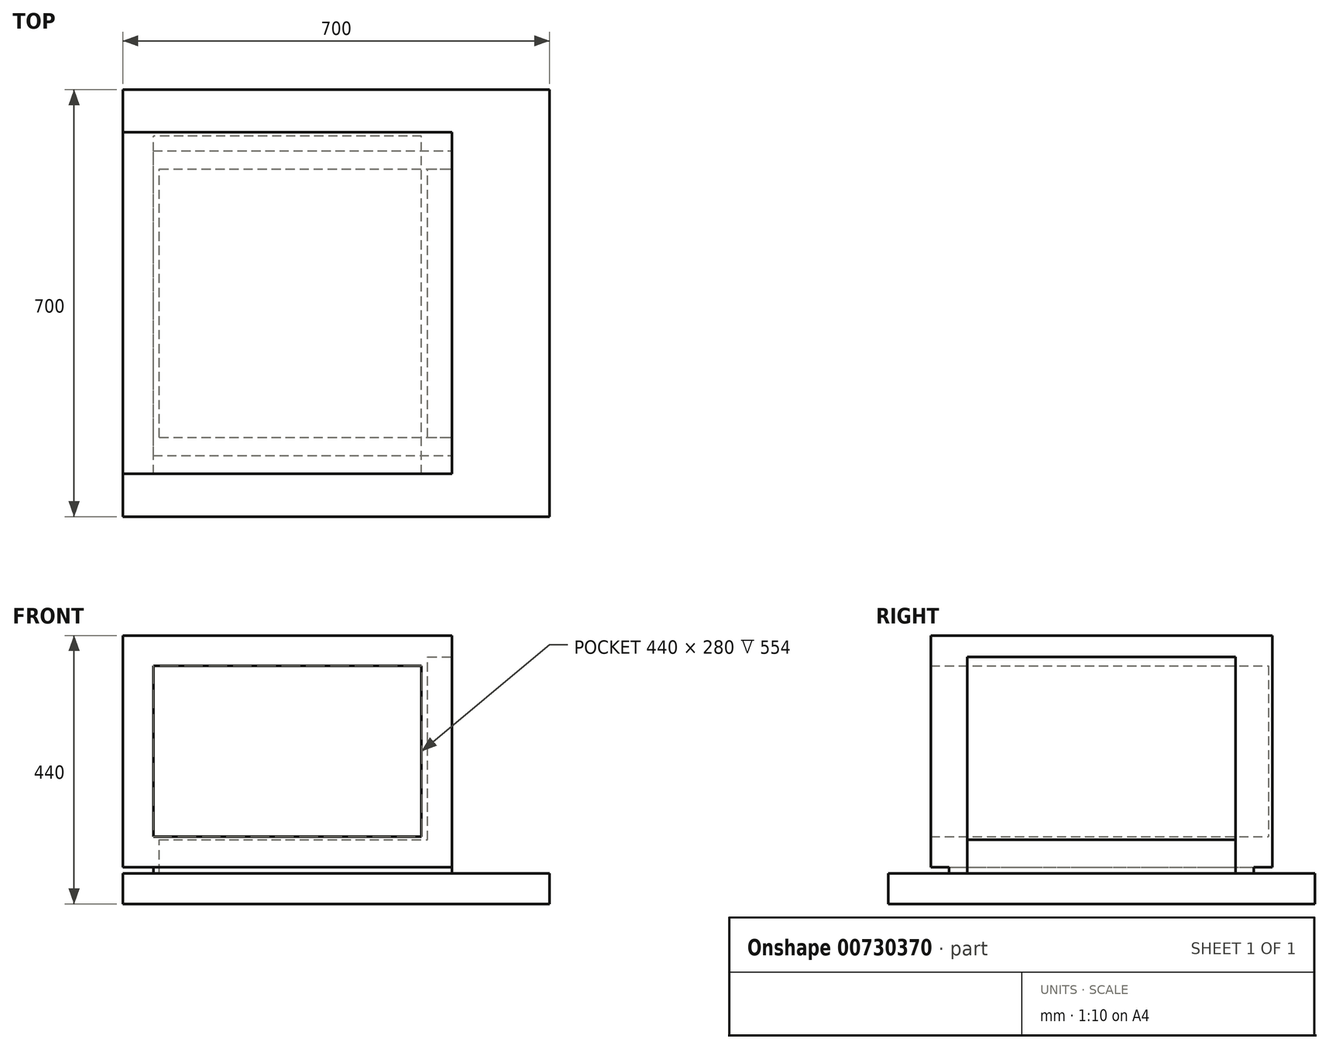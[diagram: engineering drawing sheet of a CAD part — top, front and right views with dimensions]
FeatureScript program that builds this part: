
annotation { "Feature Type Name" : "Feature", "Feature Type Description" : "" }
export const myFeature = defineFeature(function(context is Context, id is Id, definition is map)
    precondition{}
    {
        {
            var Q0;
            Q0=qCreatedBy(makeId("Front.planeOp"),FACE);
            var sketch = newSketch(context, id + "F0", { "sketchPlane" : qUnion([Q0])});
            skLineSegment(sketch, "E0.bottom", {"start": v(-270, 190) * mm, "end": v(270, 190) * mm});
            skLineSegment(sketch, "E0.top", {"start": v(-270, -190) * mm, "end": v(270, -190) * mm});
            skLineSegment(sketch, "E0.left", {"start": v(-270, 190) * mm, "end": v(-270, -190) * mm});
            skLineSegment(sketch, "E0.right", {"start": v(270, 190) * mm, "end": v(270, -190) * mm});
            skPoint(sketch, "E0.middle", {"position": v(0, 0) * mm});
            skLineSegment(sketch, "E1.bottom", {"start": v(220, 140) * mm, "end": v(-220, 140) * mm});
            skLineSegment(sketch, "E1.top", {"start": v(220, -140) * mm, "end": v(-220, -140) * mm});
            skLineSegment(sketch, "E1.left", {"start": v(220, 140) * mm, "end": v(220, -140) * mm});
            skLineSegment(sketch, "E1.right", {"start": v(-220, 140) * mm, "end": v(-220, -140) * mm});
            skSolve(sketch);
        }
        {
            var Q0;
            Q0 = qSketchRegion(id + "F0", true);
            extrude(context, id + "F1", {"entities" : qUnion([Q0]), "depth" : 560 * mm, "offsetDistance" : 25 * mm});
        }
        {
            var Q0;
            Q0=makeQuery(id+"F1.opExtrude","SWEPT_FACE",FACE,{"disambiguationData":[OSD([sQuery(id+"F0.wireOp",EDGE,"E0.top")])]});
            var sketch = newSketch(context, id + "F2", { "sketchPlane" : qUnion([Q0])});
            skLineSegment(sketch, "E2.bottom", {"start": v(-220, 530) * mm, "end": v(270, 530) * mm});
            skLineSegment(sketch, "E2.top", {"start": v(-220, 30) * mm, "end": v(270, 30) * mm});
            skLineSegment(sketch, "E2.left", {"start": v(-220, 530) * mm, "end": v(-220, 30) * mm});
            skLineSegment(sketch, "E2.right", {"start": v(270, 530) * mm, "end": v(270, 30) * mm});
            skSolve(sketch);
        }
        {
            var Q0;
            Q0 = qSketchRegion(id + "F2", true);
            extrude(context, id + "F3", {"entities" : qUnion([Q0]), "operationType" : NewBodyOperationType.ADD, "depth" : 10 * mm, "offsetDistance" : 25 * mm});
        }
        {
            var Q0;
            Q0=makeQuery(id+"F3.opExtrude","CAP_FACE",FACE,{"disambiguationData":[OSD([sQuery(id+"F2.wireOp",EDGE,"E2.bottom"),sQuery(id+"F2.wireOp",EDGE,"E2.top"),sQuery(id+"F2.wireOp",EDGE,"E2.left"),sQuery(id+"F2.wireOp",EDGE,"E2.right")])],"isStart":false});
            var sketch = newSketch(context, id + "F4", { "sketchPlane" : qUnion([Q0])});
            skLineSegment(sketch, "E3.bottom", {"start": v(-270, 630) * mm, "end": v(430, 630) * mm});
            skLineSegment(sketch, "E3.top", {"start": v(-270, -70) * mm, "end": v(430, -70) * mm});
            skLineSegment(sketch, "E3.left", {"start": v(-270, 630) * mm, "end": v(-270, -70) * mm});
            skLineSegment(sketch, "E3.right", {"start": v(430, 630) * mm, "end": v(430, -70) * mm});
            skLineSegment(sketch, "E4", {"start": v(270, 630) * mm, "end": v(270, 530) * mm, "construction": true});
            skLineSegment(sketch, "E5", {"start": v(270, 30) * mm, "end": v(270, -70) * mm, "construction": true});
            skSolve(sketch);
        }
        {
            var Q0;
            Q0 = qSketchRegion(id + "F4", true);
            extrude(context, id + "F5", {"entities" : qUnion([Q0]), "operationType" : NewBodyOperationType.ADD, "depth" : 50 * mm, "offsetDistance" : 25 * mm});
        }
        {
            var Q0;
            Q0=makeQuery(id+"F1.opExtrude","CAP_FACE",FACE,{"disambiguationData":[OSD([sQuery(id+"F0.wireOp",EDGE,"E0.bottom"),sQuery(id+"F0.wireOp",EDGE,"E0.top"),sQuery(id+"F0.wireOp",EDGE,"E0.left"),sQuery(id+"F0.wireOp",EDGE,"E0.right"),sQuery(id+"F0.wireOp",EDGE,"E1.bottom"),sQuery(id+"F0.wireOp",EDGE,"E1.top"),sQuery(id+"F0.wireOp",EDGE,"E1.left"),sQuery(id+"F0.wireOp",EDGE,"E1.right")])],"isStart":true});
            var sketch = newSketch(context, id + "F6", { "sketchPlane" : qUnion([Q0])});
            skLineSegment(sketch, "E6.bottom", {"start": v(-220, 140) * mm, "end": v(220, 140) * mm});
            skLineSegment(sketch, "E6.top", {"start": v(-220, -140) * mm, "end": v(220, -140) * mm});
            skLineSegment(sketch, "E6.left", {"start": v(-220, 140) * mm, "end": v(-220, -140) * mm});
            skLineSegment(sketch, "E6.right", {"start": v(220, 140) * mm, "end": v(220, -140) * mm});
            skSolve(sketch);
        }
        {
            var Q0;
            Q0 = qSketchRegion(id + "F6", true);
            extrude(context, id + "F7", {"entities" : qUnion([Q0]), "operationType" : NewBodyOperationType.ADD, "oppositeDirection" : true, "depth" : 6 * mm, "offsetDistance" : 25 * mm});
        }
        {
            var Q0;
            Q0=makeQuery(id+"F3.boolean.opBoolean","MERGE",FACE,{"derivedFrom":[makeQuery(id+"F1.opExtrude","SWEPT_FACE",FACE,{"disambiguationData":[OSD([sQuery(id+"F0.wireOp",EDGE,"E0.right")])]}),makeQuery(id+"F3.opExtrude","SWEPT_FACE",FACE,{"disambiguationData":[OSD([sQuery(id+"F2.wireOp",EDGE,"E2.right")])]})]});
            var sketch = newSketch(context, id + "F8", { "sketchPlane" : qUnion([Q0])});
            skLineSegment(sketch, "E7.bottom", {"start": v(-500, -200) * mm, "end": v(-60, -200) * mm});
            skLineSegment(sketch, "E7.top", {"start": v(-500, -145) * mm, "end": v(-60, -145) * mm});
            skLineSegment(sketch, "E7.left", {"start": v(-500, -200) * mm, "end": v(-500, -145) * mm});
            skLineSegment(sketch, "E7.right", {"start": v(-60, -200) * mm, "end": v(-60, -145) * mm});
            skSolve(sketch);
        }
        {
            var Q0;
            Q0 = qSketchRegion(id + "F8", true);
            extrude(context, id + "F9", {"entities" : qUnion([Q0]), "operationType" : NewBodyOperationType.REMOVE, "oppositeDirection" : true, "depth" : 480 * mm, "offsetDistance" : 25 * mm});
        }
        {
            var Q0;
            Q0=makeQuery(id+"F3.boolean.opBoolean","MERGE",FACE,{"derivedFrom":[makeQuery(id+"F1.opExtrude","SWEPT_FACE",FACE,{"disambiguationData":[OSD([sQuery(id+"F0.wireOp",EDGE,"E0.right")])]}),makeQuery(id+"F3.opExtrude","SWEPT_FACE",FACE,{"disambiguationData":[OSD([sQuery(id+"F2.wireOp",EDGE,"E2.right")])]})]});
            var sketch = newSketch(context, id + "F10", { "sketchPlane" : qUnion([Q0])});
            skLineSegment(sketch, "E8.bottom", {"start": v(-500, -145) * mm, "end": v(-60, -145) * mm});
            skLineSegment(sketch, "E8.top", {"start": v(-500, 155) * mm, "end": v(-60, 155) * mm});
            skLineSegment(sketch, "E8.left", {"start": v(-500, -145) * mm, "end": v(-500, 155) * mm});
            skLineSegment(sketch, "E8.right", {"start": v(-60, -145) * mm, "end": v(-60, 155) * mm});
            skSolve(sketch);
        }
        {
            var Q0;
            Q0 = qSketchRegion(id + "F10", true);
            extrude(context, id + "F11", {"entities" : qUnion([Q0]), "operationType" : NewBodyOperationType.REMOVE, "oppositeDirection" : true, "depth" : 40 * mm, "offsetDistance" : 25 * mm});
        }
    });
